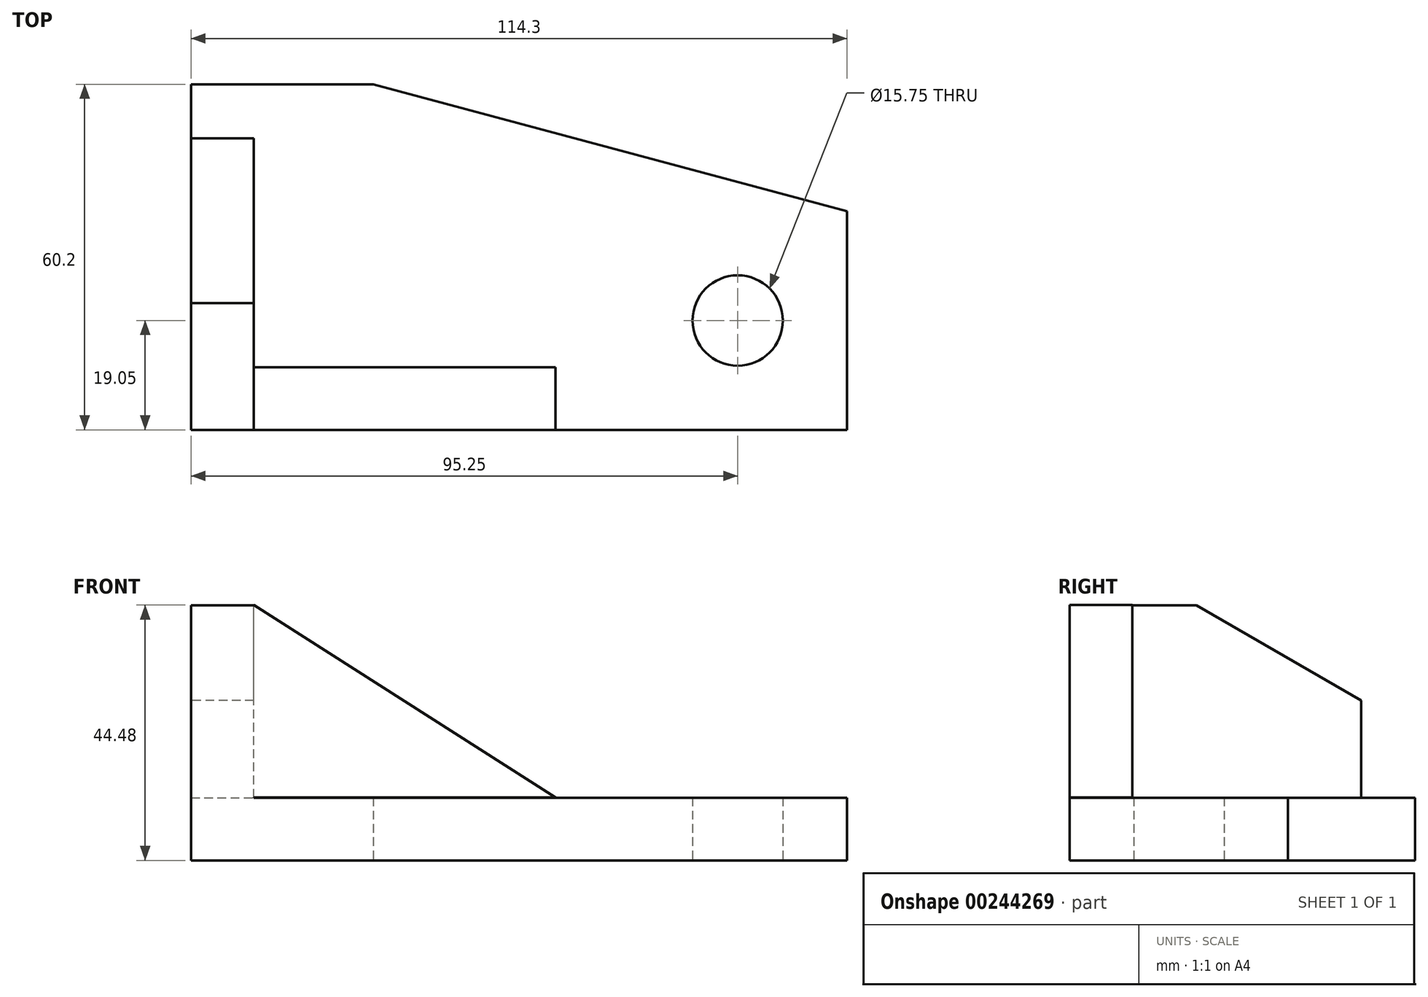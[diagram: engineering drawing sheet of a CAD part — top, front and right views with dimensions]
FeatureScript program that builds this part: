
annotation { "Feature Type Name" : "Feature", "Feature Type Description" : "" }
export const myFeature = defineFeature(function(context is Context, id is Id, definition is map)
    precondition{}
    {
        {
            var Q0;
            Q0=qCreatedBy(makeId("Top.planeOp"),FACE);
            var sketch = newSketch(context, id + "F0", { "sketchPlane" : qUnion([Q0])});
            skLineSegment(sketch, "E0.bottom", {"start": v(0, 0) * mm, "end": v(114.3, 0) * mm});
            skLineSegment(sketch, "E0.top", {"start": v(0, 60.2) * mm, "end": v(114.3, 60.2) * mm});
            skLineSegment(sketch, "E0.left", {"start": v(0, 0) * mm, "end": v(0, 60.2) * mm});
            skLineSegment(sketch, "E0.right", {"start": v(114.3, 0) * mm, "end": v(114.3, 60.2) * mm});
            skLineSegment(sketch, "E1", {"start": v(0, 60.2) * mm, "end": v(31.75, 60.2) * mm});
            skLineSegment(sketch, "E2", {"start": v(31.75, 60.2) * mm, "end": v(114.3, 38.08) * mm});
            skLineSegment(sketch, "E3", {"start": v(114.3, 0) * mm, "end": v(95.25, 0) * mm});
            skLineSegment(sketch, "E4", {"start": v(95.25, 0) * mm, "end": v(95.25, 19.05) * mm});
            skSolve(sketch);
        }
        {
            var Q0;
            Q0=qCreatedBy(makeId("Right.planeOp"),FACE);
            var sketch = newSketch(context, id + "F1", { "sketchPlane" : qUnion([Q0])});
            skLineSegment(sketch, "E5", {"start": v(0, 0) * mm, "end": v(0, 44.45) * mm});
            skLineSegment(sketch, "E6", {"start": v(0, 44.45) * mm, "end": v(22.1, 44.45) * mm});
            skLineSegment(sketch, "E7", {"start": v(0, 0) * mm, "end": v(50.8, 0) * mm});
            skLineSegment(sketch, "E8", {"start": v(50.8, 0) * mm, "end": v(50.8, 27.88) * mm});
            skLineSegment(sketch, "E9", {"start": v(50.8, 27.88) * mm, "end": v(22.1, 44.45) * mm});
            skSolve(sketch);
        }
        {
            var Q0;
            Q0=qCreatedBy(makeId("Front.planeOp"),FACE);
            var sketch = newSketch(context, id + "F2", { "sketchPlane" : qUnion([Q0])});
            skLineSegment(sketch, "E10", {"start": v(0, 44.48) * mm, "end": v(63.5, 44.48) * mm});
            skLineSegment(sketch, "E11", {"start": v(63.5, 44.48) * mm, "end": v(63.5, 10.95) * mm});
            skLineSegment(sketch, "E12", {"start": v(0, 44.48) * mm, "end": v(10.92, 44.48) * mm});
            skLineSegment(sketch, "E13", {"start": v(10.92, 44.48) * mm, "end": v(63.5, 10.95) * mm});
            skLineSegment(sketch, "E14", {"start": v(10.92, 10.95) * mm, "end": v(10.92, 44.48) * mm});
            skLineSegment(sketch, "E15", {"start": v(10.92, 10.95) * mm, "end": v(63.5, 10.95) * mm});
            skLineSegment(sketch, "E16", {"start": v(0, 10.95) * mm, "end": v(63.5, 10.95) * mm});
            skSolve(sketch);
        }
        {
            var Q0;
            Q0=makeQuery(id+"F0.imprint","IMPRINT",FACE,{"disambiguationData":[TD([[makeQuery(id+"F0.imprint","IMPRINT",EDGE,{"derivedFrom":sQuery(id+"F0.wireOp",EDGE,"E0.bottom")}),1.0]])]});
            extrude(context, id + "F3", {"entities" : qUnion([Q0]), "depth" : 10.92 * mm});
        }
        {
            var Q0;
            Q0=sQuery(id+"F0.wireOp",VERTEX,"E4.end");
            var Q1;
            Q1=makeQuery(id+"F3.opExtrude","SWEPT_BODY",BODY,{"disambiguationData":[OSD([sQuery(id+"F0.wireOp",EDGE,"E0.bottom"),sQuery(id+"F0.wireOp",EDGE,"E0.left"),sQuery(id+"F0.wireOp",EDGE,"E0.right"),sQuery(id+"F0.wireOp",EDGE,"E1"),sQuery(id+"F0.wireOp",EDGE,"E2"),sQuery(id+"F0.wireOp",EDGE,"E3")])]});
            hole(context, id + "F4", {"style" : HoleStyle.SIMPLE, "endStyle" : HoleEndStyle.THROUGH, "oppositeDirection" : true, "holeDiameter" : 15.75 * mm, "locations" : qUnion([Q0]), "scope" : qUnion([Q1]), "isTappedThrough" : true});
        }
        {
            var Q0;
            Q0=makeQuery(id+"F1.imprint","IMPRINT",FACE,{"disambiguationData":[TD([[makeQuery(id+"F1.imprint","IMPRINT",EDGE,{"derivedFrom":sQuery(id+"F1.wireOp",EDGE,"E5")}),-1.0]])]});
            extrude(context, id + "F5", {"entities" : qUnion([Q0]), "operationType" : NewBodyOperationType.ADD, "depth" : 10.92 * mm});
        }
        {
            var Q0;
            Q0=makeQuery(id+"F2.imprint","IMPRINT",FACE,{"disambiguationData":[TD([[makeQuery(id+"F2.imprint","IMPRINT",EDGE,{"derivedFrom":sQuery(id+"F2.wireOp",EDGE,"E13")}),-1.0]])]});
            extrude(context, id + "F6", {"entities" : qUnion([Q0]), "operationType" : NewBodyOperationType.ADD, "oppositeDirection" : true, "depth" : 10.92 * mm});
        }
    });
